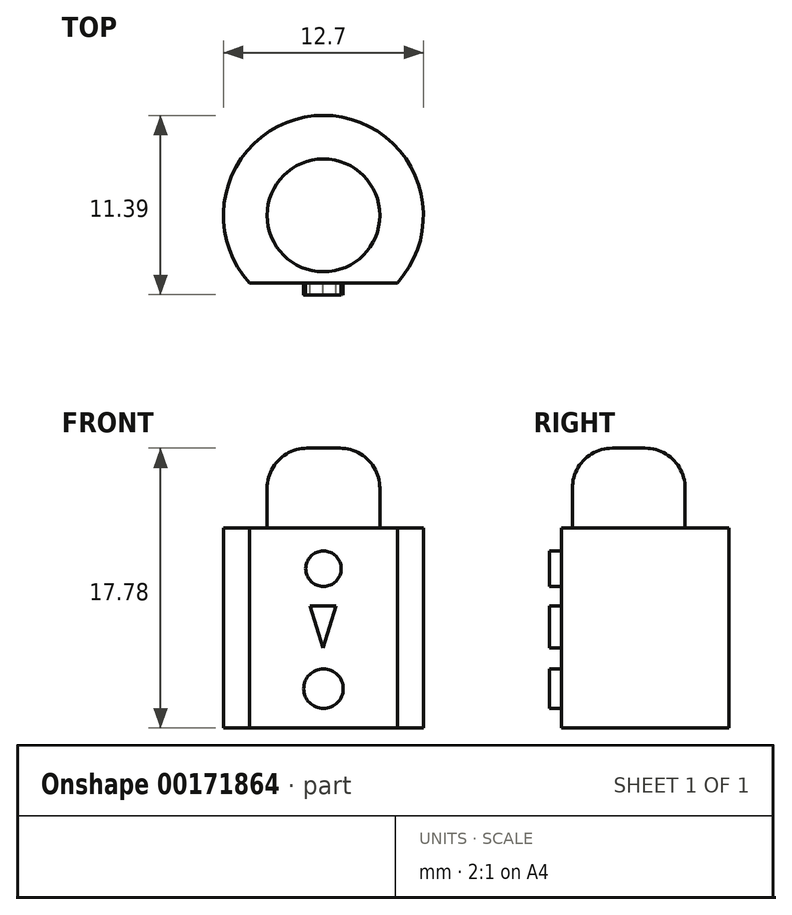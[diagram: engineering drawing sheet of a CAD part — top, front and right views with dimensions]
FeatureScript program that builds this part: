
annotation { "Feature Type Name" : "Feature", "Feature Type Description" : "" }
export const myFeature = defineFeature(function(context is Context, id is Id, definition is map)
    precondition{}
    {
        {
            var Q0;
            Q0=qCreatedBy(makeId("Top.planeOp"),FACE);
            var sketch = newSketch(context, id + "F0", { "sketchPlane" : qUnion([Q0])});
            skArc(sketch, "E0", {"start": v(4.69, -4.28) * mm, "mid": v(0, 6.35) * mm, "end": v(-4.69, -4.28) * mm});
            skLineSegment(sketch, "E1", {"start": v(4.69, -4.28) * mm, "end": v(-4.69, -4.28) * mm});
            skSolve(sketch);
        }
        {
            var Q0;
            Q0=makeQuery(id+"F0.imprint","IMPRINT",FACE,{"disambiguationData":[TD([[makeQuery(id+"F0.imprint","IMPRINT",EDGE,{"derivedFrom":sQuery(id+"F0.wireOp",EDGE,"E0")}),1.0]])]});
            extrude(context, id + "F1", {"entities" : qUnion([Q0]), "depth" : 12.7 * mm});
        }
        {
            var Q0;
            Q0=makeQuery(id+"F1.opExtrude","CAP_FACE",FACE,{"disambiguationData":[OSD([sQuery(id+"F0.wireOp",EDGE,"E0")])],"isStart":false});
            var sketch = newSketch(context, id + "F2", { "sketchPlane" : qUnion([Q0])});
            skCircle(sketch, "E2", {"center": v(0, 0) * mm, "radius": 3.58 * mm});
            skSolve(sketch);
        }
        {
            var Q0;
            Q0=makeQuery(id+"F2.imprint","IMPRINT",FACE,{"disambiguationData":[TD([[makeQuery(id+"F2.imprint","IMPRINT",EDGE,{"derivedFrom":sQuery(id+"F2.wireOp",EDGE,"E2")}),1.0]])]});
            extrude(context, id + "F3", {"entities" : qUnion([Q0]), "depth" : 5.08 * mm});
        }
        {
            var Q0;
            Q0=makeQuery(id+"F3.opExtrude","CAP_EDGE",EDGE,{"disambiguationData":[OSD([sQuery(id+"F2.wireOp",EDGE,"E2")])],"isStart":false});
            fillet(context, id + "F4", {"entities" : qUnion([Q0]), "radius" : 2.54 * mm, "tangentPropagation" : true, "allowEdgeOverflow" : false});
        }
        {
            var Q0;
            Q0=makeQuery(id+"F1.opExtrude","SWEPT_FACE",FACE,{"disambiguationData":[OSD([sQuery(id+"F0.wireOp",EDGE,"E1")])]});
            var sketch = newSketch(context, id + "F5", { "sketchPlane" : qUnion([Q0])});
            skCircle(sketch, "E3", {"center": v(0, 10.13) * mm, "radius": 1.13 * mm});
            skPoint(sketch, "E4.center.orphan", {"position": v(0, 2.33) * mm});
            skSolve(sketch);
        }
        {
            var Q0;
            Q0=makeQuery(id+"F5.imprint","IMPRINT",FACE,{"disambiguationData":[TD([[makeQuery(id+"F5.imprint","IMPRINT",EDGE,{"derivedFrom":sQuery(id+"F5.wireOp",EDGE,"E3")}),1.0]])]});
            extrude(context, id + "F6", {"entities" : qUnion([Q0]), "depth" : 0.76 * mm});
        }
        {
            var Q0;
            Q0=makeQuery(id+"F1.opExtrude","SWEPT_FACE",FACE,{"disambiguationData":[OSD([sQuery(id+"F0.wireOp",EDGE,"E1")])]});
            var sketch = newSketch(context, id + "F7", { "sketchPlane" : qUnion([Q0])});
            skCircle(sketch, "E5", {"center": v(0, 2.5) * mm, "radius": 1.25 * mm});
            skSolve(sketch);
        }
        {
            var Q0;
            Q0=makeQuery(id+"F7.imprint","IMPRINT",FACE,{"disambiguationData":[TD([[makeQuery(id+"F7.imprint","IMPRINT",EDGE,{"derivedFrom":sQuery(id+"F7.wireOp",EDGE,"E5")}),1.0]])]});
            extrude(context, id + "F8", {"entities" : qUnion([Q0]), "depth" : 0.76 * mm});
        }
        {
            var Q0;
            Q0=makeQuery(id+"F1.opExtrude","SWEPT_FACE",FACE,{"disambiguationData":[OSD([sQuery(id+"F0.wireOp",EDGE,"E1")])]});
            var sketch = newSketch(context, id + "F9", { "sketchPlane" : qUnion([Q0])});
            skLineSegment(sketch, "E6.top", {"start": v(-0.86, 7.75) * mm, "end": v(0.8, 7.75) * mm});
            skLineSegment(sketch, "E7", {"start": v(0.8, 7.75) * mm, "end": v(-0.03, 5.08) * mm});
            skLineSegment(sketch, "E8", {"start": v(-0.03, 5.08) * mm, "end": v(-0.86, 7.75) * mm});
            skPoint(sketch, "E9.orphan", {"position": v(-0.86, 5.08) * mm});
            skPoint(sketch, "E6.bottom.end.orphan", {"position": v(0.8, 5.08) * mm});
            skSolve(sketch);
        }
        {
            var Q0;
            Q0=makeQuery(id+"F9.imprint","IMPRINT",FACE,{"disambiguationData":[TD([[makeQuery(id+"F9.imprint","IMPRINT",EDGE,{"derivedFrom":sQuery(id+"F9.wireOp",EDGE,"E6.top")}),-1.0]])]});
            extrude(context, id + "F10", {"entities" : qUnion([Q0]), "depth" : 0.76 * mm});
        }
    });
